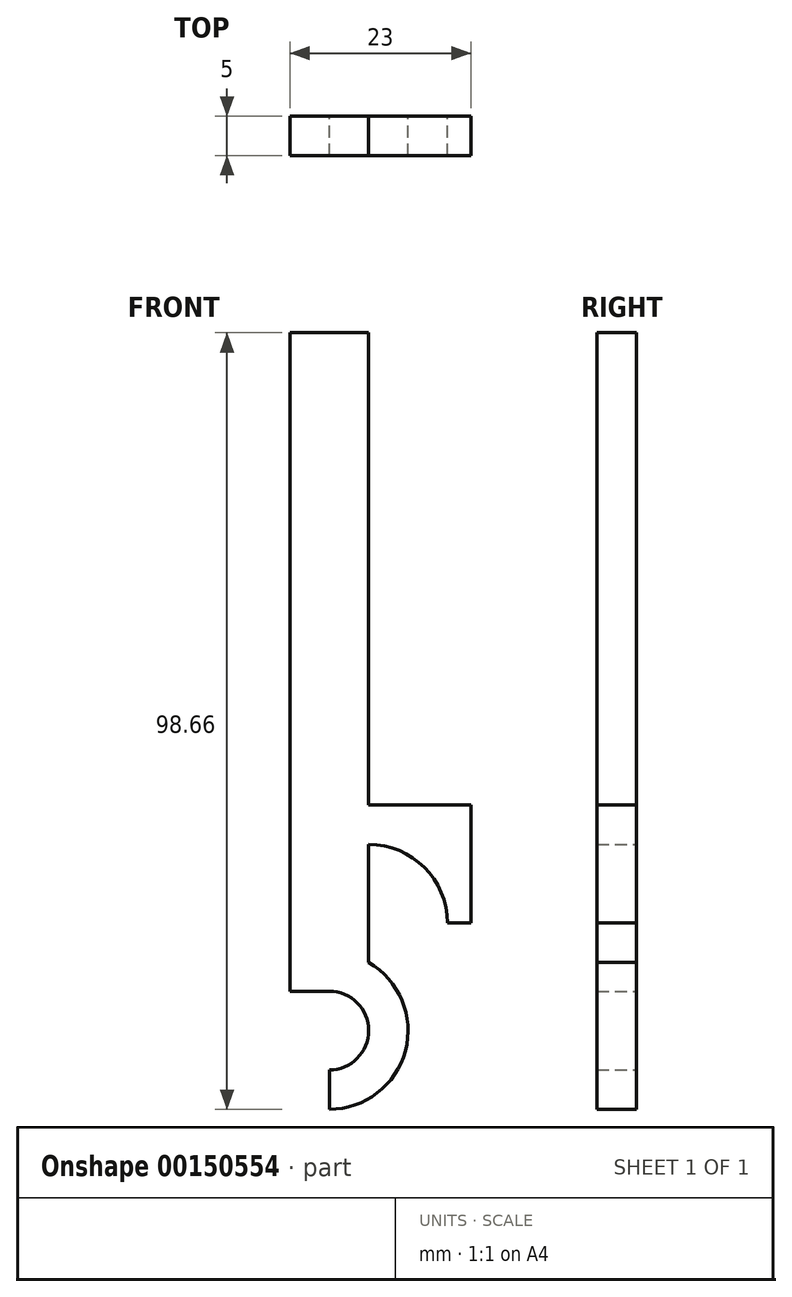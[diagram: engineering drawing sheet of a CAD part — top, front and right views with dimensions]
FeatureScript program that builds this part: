
annotation { "Feature Type Name" : "Feature", "Feature Type Description" : "" }
export const myFeature = defineFeature(function(context is Context, id is Id, definition is map)
    precondition{}
    {
        {
            var Q0;
            Q0=qCreatedBy(makeId("Front.planeOp"),FACE);
            var sketch = newSketch(context, id + "F0", { "sketchPlane" : qUnion([Q0])});
            skLineSegment(sketch, "E0.top", {"start": v(5, 44.33) * mm, "end": v(-5, 44.33) * mm});
            skLineSegment(sketch, "E0.left", {"start": v(5, -35.67) * mm, "end": v(5, 44.33) * mm});
            skLineSegment(sketch, "E0.right", {"start": v(-5, -35.67) * mm, "end": v(-5, 44.33) * mm});
            skPoint(sketch, "E0.middle", {"position": v(0, 0) * mm});
            skArc(sketch, "E1", {"start": v(0, -49.33) * mm, "mid": v(5, -44.33) * mm, "end": v(0, -39.33) * mm});
            skArc(sketch, "E2", {"start": v(0, -54.33) * mm, "mid": v(10, -44.33) * mm, "end": v(0, -34.33) * mm});
            skLineSegment(sketch, "E3", {"start": v(0, -34.33) * mm, "end": v(0, -39.33) * mm});
            skPoint(sketch, "E4.orphan", {"position": v(-5, -44.33) * mm});
            skLineSegment(sketch, "E5.trimOffspring", {"start": v(0, -49.33) * mm, "end": v(0, -54.33) * mm});
            skPoint(sketch, "E6.orphan", {"position": v(5, -44.33) * mm});
            skLineSegment(sketch, "E7", {"start": v(-5, -35.67) * mm, "end": v(-5, -39.33) * mm});
            skLineSegment(sketch, "E8", {"start": v(-5, -39.33) * mm, "end": v(0, -39.33) * mm});
            skLineSegment(sketch, "E9.left", {"start": v(5, -30.67) * mm, "end": v(5, -20.67) * mm});
            skArc(sketch, "E10", {"start": v(15, -30.67) * mm, "mid": v(12.07, -23.6) * mm, "end": v(5, -20.67) * mm});
            skLineSegment(sketch, "E11", {"start": v(5, -15.67) * mm, "end": v(18, -15.67) * mm});
            skLineSegment(sketch, "E12", {"start": v(18, -15.67) * mm, "end": v(18, -30.67) * mm});
            skLineSegment(sketch, "E13", {"start": v(18, -30.67) * mm, "end": v(15, -30.67) * mm});
            skSolve(sketch);
        }
        {
            var Q0;
            Q0 = qSketchRegion(id + "F0", true);
            extrude(context, id + "F1", {"entities" : qUnion([Q0]), "depth" : 5 * mm});
        }
    });
